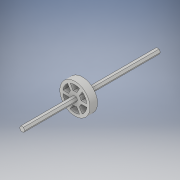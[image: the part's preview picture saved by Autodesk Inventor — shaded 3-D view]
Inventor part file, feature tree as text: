
AUTODESK INVENTOR PART (.ipt)
format: ipt  version: 2018 (Build 220112000, 112)  size: 200,704 bytes
history: native  units: in
note: dims shown in document units (in); Inventor stores cm internally (conversion verified against a paired STEP export)
features: extrude x2, sketch x2, plane x1, projected_geometry x1
ambient origin geometry x8: Origin, YZ Plane, XZ Plane, XY Plane, X Axis, Y Axis, Z Axis, Center Point
bodies: Solid1 (feature_tree)
feature tree (6):
  extrude  "Extrusion1"  Depth=9.0in TaperAngle=0.0deg
  plane  "Work Plane1"
  extrude  "Extrusion3"  Depth=0.5in
  sketch  "Sketch1"  dims[d0=0.3in d1=9.0in d2=0.0in]
  sketch  "Sketch2"  dims[d3=-4.0in d4=2.0in d5=0.2in d6=0.85in d31=0.2in d32=0.1in d33=0.2in d34=0.1in d35=120.0deg d36=120.0deg d37=120.0deg d38=120.0deg d39=0.2in d40=0.1in d41=0.2in d42=0.1in d44=0.2in d45=0.1in d46=0.2in d47=0.1in d48=0.5in d49=0.0in]
  projected_geometry  "Projected Loop1"
